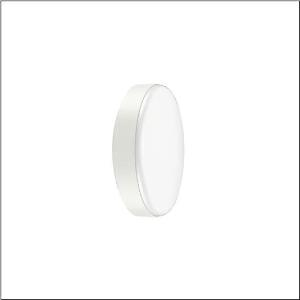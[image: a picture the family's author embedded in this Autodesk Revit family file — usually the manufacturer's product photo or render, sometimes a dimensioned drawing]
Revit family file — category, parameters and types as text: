
# Revit family: rondel_31_51wc10da42as
name_source: partatom
category: Lighting Fixtures
units: mm (PartAtom-declared; Revit-internal decimal feet)

## family parameters
Cut with Voids When Loaded = No
Host = Face
Light Source = No
Part Type = Normal
Room Calculation Point = No
Round Connector Dimension = Use Diameter
Shared = No

## types (1)
- Rondel 31 (1 x LED, 2550 lm, 20.5 W, 4000K)
    Apparent Load = 21 VA
    CIE Flux Codes = 44 75 94 94 100
    Color Rendering = 80
    Color Temperature = 4000K
    Default Elevation = 1800 mm
    Description = Rondel 31, wall and ceiling luminaire, primary optical cover: cover, of PC, opal, light emission: direct distribution, primary light characteristic: symmetric, installation type: surface-mounted, LED, rated luminous flux: 2.550lm, luminous efficacy: 124lm/W, light colour: 840, colour temperature: 4000K, with terminal, 5-pole, max. 2.5mm², mains connection: 220..240V, AC, 50/60Hz, rated input power: 20.5W, luminaire housing, of PC, traffic white (RAL 9016), diameter: 350mm, brightness and presence sensor, HF sensor, protection rating (complete): IP65, insulation class (complete): insulation class II (safety insulation), certification: CE, impact resistance: IK10, permissible operating ambient temperature: -20..+40°C, permissible storage temperature: -20..+60°C, packaging unit: 1 piece
    Height = 97 mm
    Lamp = 1 x LED
    Lamp Light Flux = 2550 lm
    Lamp Power = 20.5 W
    Lamp count = 1
    Length = 350 mm
    Luminous efficacy = 124 lm/W
    Manufacturer = Siteco
    ModVariant = No
    Model = 51WC10DA42AS
    Mounting Place = Ceiling
    Mounting Type = Surface mounted
    Number of Poles = 1
    OnlyDefault = Yes
    Power Factor = 1
    Product Name = Rondel 31
    Product group = wall and ceiling luminaire
    ProductGroupID = 301
    Protection Class = Protection class II
    Protection Degree = IP 65
    RLX_Detail_Level = 1
    RLX_Emergency_Light_Flux = 0 lm
    RLX_Emergency_Type = 0
    RLX_Emergency_Type_DB = No
    RlxData = <blob elided: 29693 chars, md5=dccc1d21>
    Socket = socket
    Standby Power = 0 W
    System Light Flux = 2550 lm
    System Power = 21 W
    Type Comments = Product without accessories
    Type Image = l_1007027.jpg
    URL = http://relux.com
    VarID = ---
    Voltage = 0 V
    Weight = 0.00 kg
    Width = 0 mm  [stored 0 ft]

note: [stored X ft] marks values corroborated as IEEE doubles in the binary element streams (Revit-internal decimal feet)

## geometry (parser evidence)
native form markers: Blend x4, Sweep x13
no freeform markers — native parametric forms only
